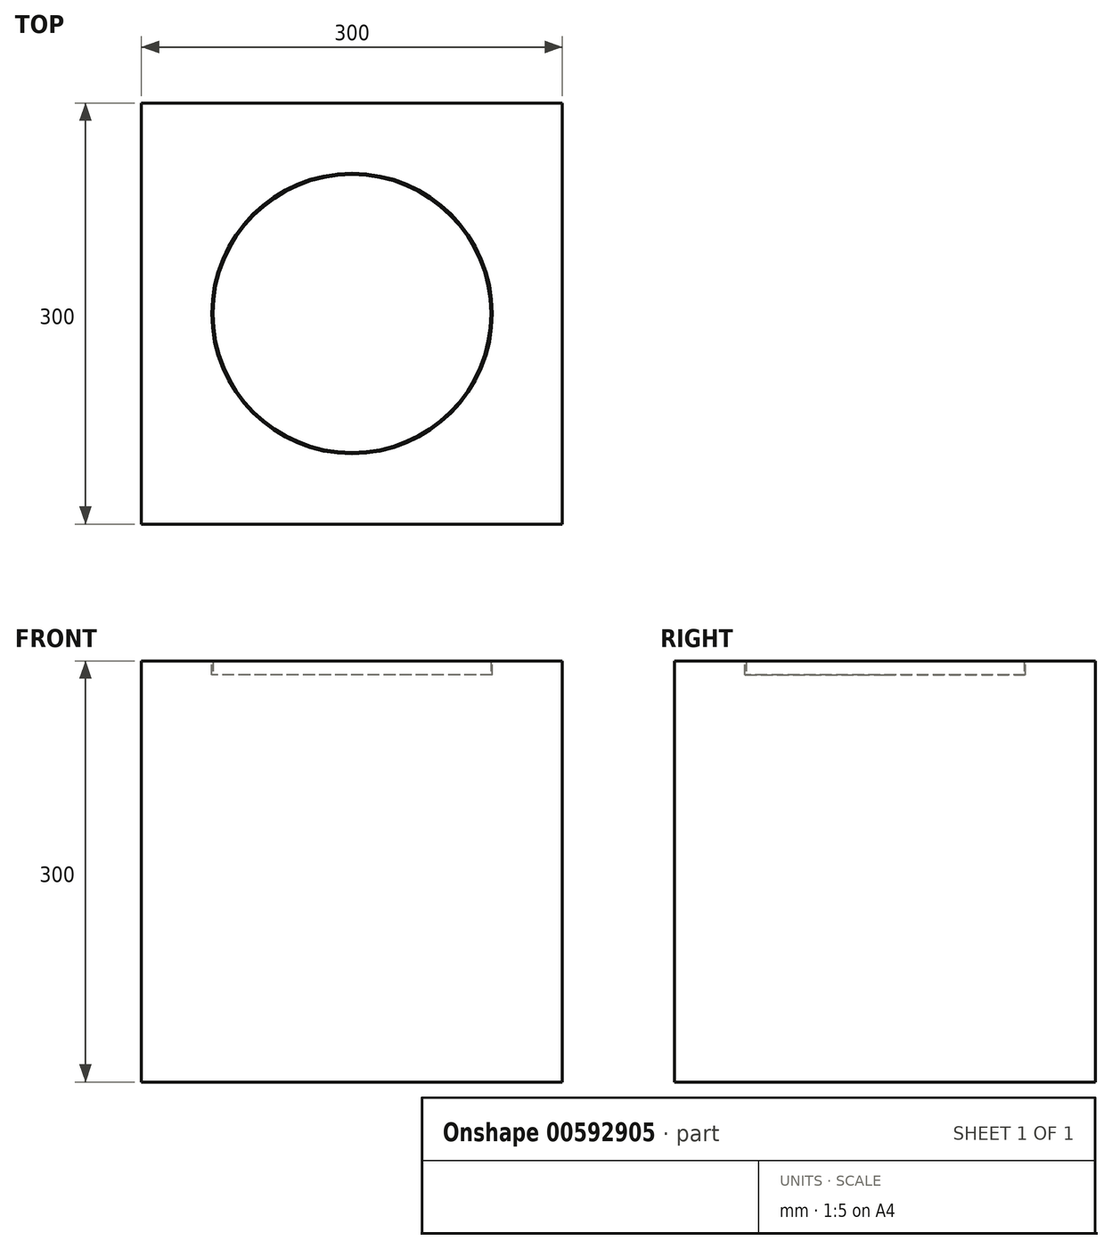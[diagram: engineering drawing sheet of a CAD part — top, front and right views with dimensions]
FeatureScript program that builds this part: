
annotation { "Feature Type Name" : "Feature", "Feature Type Description" : "" }
export const myFeature = defineFeature(function(context is Context, id is Id, definition is map)
    precondition{}
    {
        {
            var Q0;
            Q0=qCreatedBy(makeId("Top.planeOp"),FACE);
            var sketch = newSketch(context, id + "F0", { "sketchPlane" : qUnion([Q0])});
            skLineSegment(sketch, "E0.bottom", {"start": v(150, -150) * mm, "end": v(-150, -150) * mm});
            skLineSegment(sketch, "E0.top", {"start": v(150, 150) * mm, "end": v(-150, 150) * mm});
            skLineSegment(sketch, "E0.left", {"start": v(150, -150) * mm, "end": v(150, 150) * mm});
            skLineSegment(sketch, "E0.right", {"start": v(-150, -150) * mm, "end": v(-150, 150) * mm});
            skPoint(sketch, "E0.middle", {"position": v(0, 0) * mm});
            skSolve(sketch);
        }
        {
            var Q0;
            Q0 = qSketchRegion(id + "F0", true);
            extrude(context, id + "F1", {"entities" : qUnion([Q0]), "endBound" : BoundingType.SYMMETRIC, "depth" : 300 * mm, "offsetDistance" : 25 * mm});
        }
        {
            var Q0;
            Q0=makeQuery(id+"F1.opExtrude","CAP_FACE",FACE,{"disambiguationData":[OSD([sQuery(id+"F0.wireOp",EDGE,"E0.bottom"),sQuery(id+"F0.wireOp",EDGE,"E0.top"),sQuery(id+"F0.wireOp",EDGE,"E0.left"),sQuery(id+"F0.wireOp",EDGE,"E0.right")])],"isStart":false});
            var sketch = newSketch(context, id + "F2", { "sketchPlane" : qUnion([Q0])});
            skCircle(sketch, "E1", {"center": v(0, 0) * mm, "radius": 100 * mm});
            skSolve(sketch);
        }
        {
            var Q0;
            Q0=makeQuery(id+"F2.imprint","IMPRINT",FACE,{"disambiguationData":[TD([[makeQuery(id+"F2.imprint","IMPRINT",EDGE,{"derivedFrom":sQuery(id+"F2.wireOp",EDGE,"E1")}),1.0]])]});
            extrude(context, id + "F3", {"entities" : qUnion([Q0]), "operationType" : NewBodyOperationType.REMOVE, "oppositeDirection" : true, "depth" : 10 * mm, "offsetDistance" : 25 * mm});
        }
        {
            var Q0;
            Q0=makeQuery(id+"F3.boolean.opBoolean","COPY",FACE,{"derivedFrom":makeQuery(id+"F3.opExtrude","CAP_FACE",FACE,{"disambiguationData":[OSD([sQuery(id+"F2.wireOp",EDGE,"E1")])],"isStart":false})});
            var sketch = newSketch(context, id + "F4", { "sketchPlane" : qUnion([Q0])});
            skCircle(sketch, "E2", {"center": v(0, 0) * mm, "radius": 99 * mm});
            skSolve(sketch);
        }
        {
            var Q0;
            Q0 = qSketchRegion(id + "F4", true);
            extrude(context, id + "F5", {"entities" : qUnion([Q0]), "operationType" : NewBodyOperationType.ADD, "depth" : 10 * mm, "offsetDistance" : 25 * mm});
        }
    });
